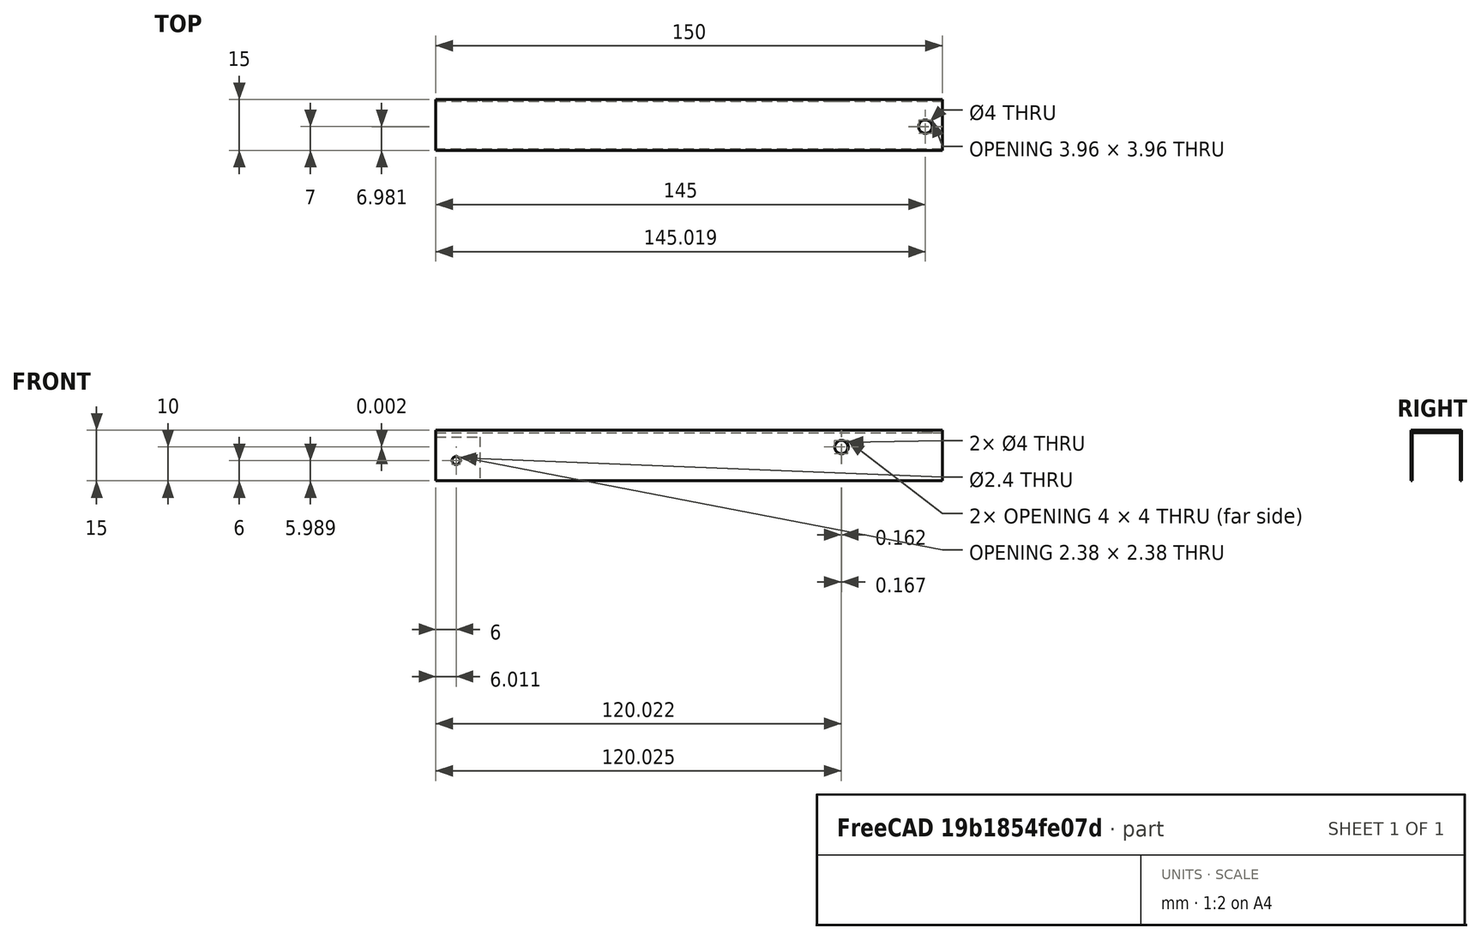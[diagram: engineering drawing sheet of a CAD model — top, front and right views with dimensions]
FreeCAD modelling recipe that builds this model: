
FCSTD DOCUMENT  (FreeCAD 0.14R3700 (Git))
Label: cutterLever
License: CC-BY 3.0
LicenseURL: http://creativecommons.org/licenses/by/3.0/
objects: Part::Cut×5, Part::Box×3, Part::Cylinder×3, Sketcher::SketchObject×1
note: 12 computed .brp shape members not serialized (recipe doc carries the construction recipe); baked Part::Feature solids carry a one-line shape summary decoded from their .brp

FEATURE [Part::Box] Box001  label="Cube001"
  Height = 15
  Length = 150
  Width = 15
FEATURE [Part::Box] Box  label="Cube"
  Height = 15
  Length = 160
  Placement = pos=(-5,0.35,-0.7) rot=(0,0,1;0rad)
  Width = 14.2
FEATURE [Part::Cut] Cut
  Base = -> Box001
  Tool = -> Box
FEATURE [Part::Cylinder] Cylinder
  Angle = 360
  Height = 5
  Placement = pos=(145,7,12) rot=(0,0,1;0rad)
  Radius = 2
FEATURE [Part::Cut] Cut001
  Base = -> Cut
  Tool = -> Cylinder
FEATURE [Part::Cylinder] Cylinder001
  Angle = 360
  Height = 20
  Placement = pos=(119.815,16.998,9.99248) rot=(0.999938,0,0.01111;1.5708rad)
  Radius = 2
FEATURE [Part::Cut] Cut002
  Base = -> Cut001
  Tool = -> Cylinder001
FEATURE [Part::Box] Box002  label="Cube002"
  Height = 13
  Length = 13
  Placement = pos=(0,12,0) rot=(0,0,1;0rad)
  Width = 5
FEATURE [Part::Cut] Cut003
  Base = -> Cut002
  Tool = -> Box002
FEATURE [Part::Cylinder] Cylinder002
  Angle = 360
  Height = 5
  Placement = pos=(6,2.5,6) rot=(1,0,0;1.5708rad)
  Radius = 1.2
FEATURE [Part::Cut] Cut004
  Base = -> Cut003
  Tool = -> Cylinder002
FEATURE [Sketcher::SketchObject] Sketch
